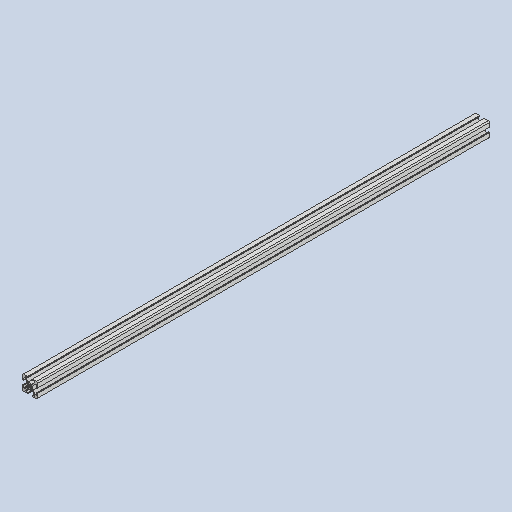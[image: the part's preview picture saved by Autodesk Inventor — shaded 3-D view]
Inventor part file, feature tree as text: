
AUTODESK INVENTOR PART (.ipt)
format: ipt  version: 2022 (Build 260153000, 153)  size: 291,328 bytes
history: native  units: in
note: dims shown in document units (in); Inventor stores cm internally (conversion verified against a paired STEP export)
features: other x3, plane x2, sketch x1
ambient origin geometry x8: Origin, YZ Plane, XZ Plane, XY Plane, X Axis, Y Axis, Z Axis, Center Point
bodies: Solid1 (feature_tree)
feature tree (6):
  other  "20x20x600 T Slot Extrusion Bar_MIR.ipt"
  other  "Solid1::20x20x600 T Slot Extrusion Bar_MIR.ipt"
  other  "TaggingFeature1"
  sketch  "Sketch_1"  dims[d0=0.3937in]
  plane  "Work Plane1"
  plane  "Work Plane2"
